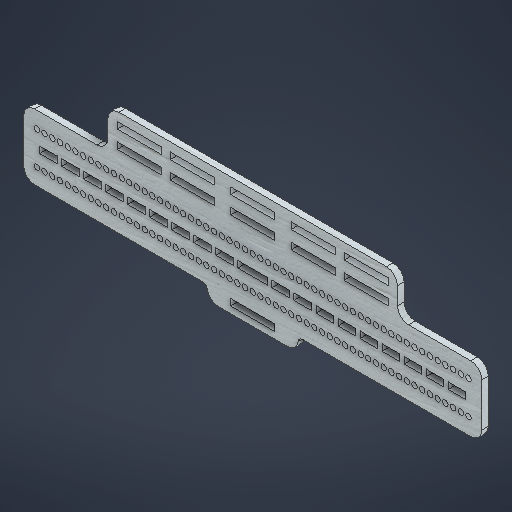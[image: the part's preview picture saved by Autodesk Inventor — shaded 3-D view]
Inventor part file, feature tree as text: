
AUTODESK INVENTOR PART (.ipt)
format: ipt  version: 2025.3 (Build 293356030, 356C)  size: 644,096 bytes
history: native  units: mm
features: other x5, sketch x3, extrude x2
ambient origin geometry x8: Origin, YZ Plane, XZ Plane, XY Plane, X Axis, Y Axis, Z Axis, Center Point
bodies: Body1 (feature_tree)
feature tree (10):
  other  "實體1"
  extrude  "擠出1"  Depth=20.0mm
  extrude  "擠出2"  Depth=3.0mm
  sketch  "草圖3"
  sketch  "草圖1"
  sketch  "草圖2"
  other  "草圖 - 矩形陣列2"
  other  "草圖 - 矩形陣列3"
  other  "草圖 - 矩形陣列4"
  other  "草圖 - 矩形陣列5"
